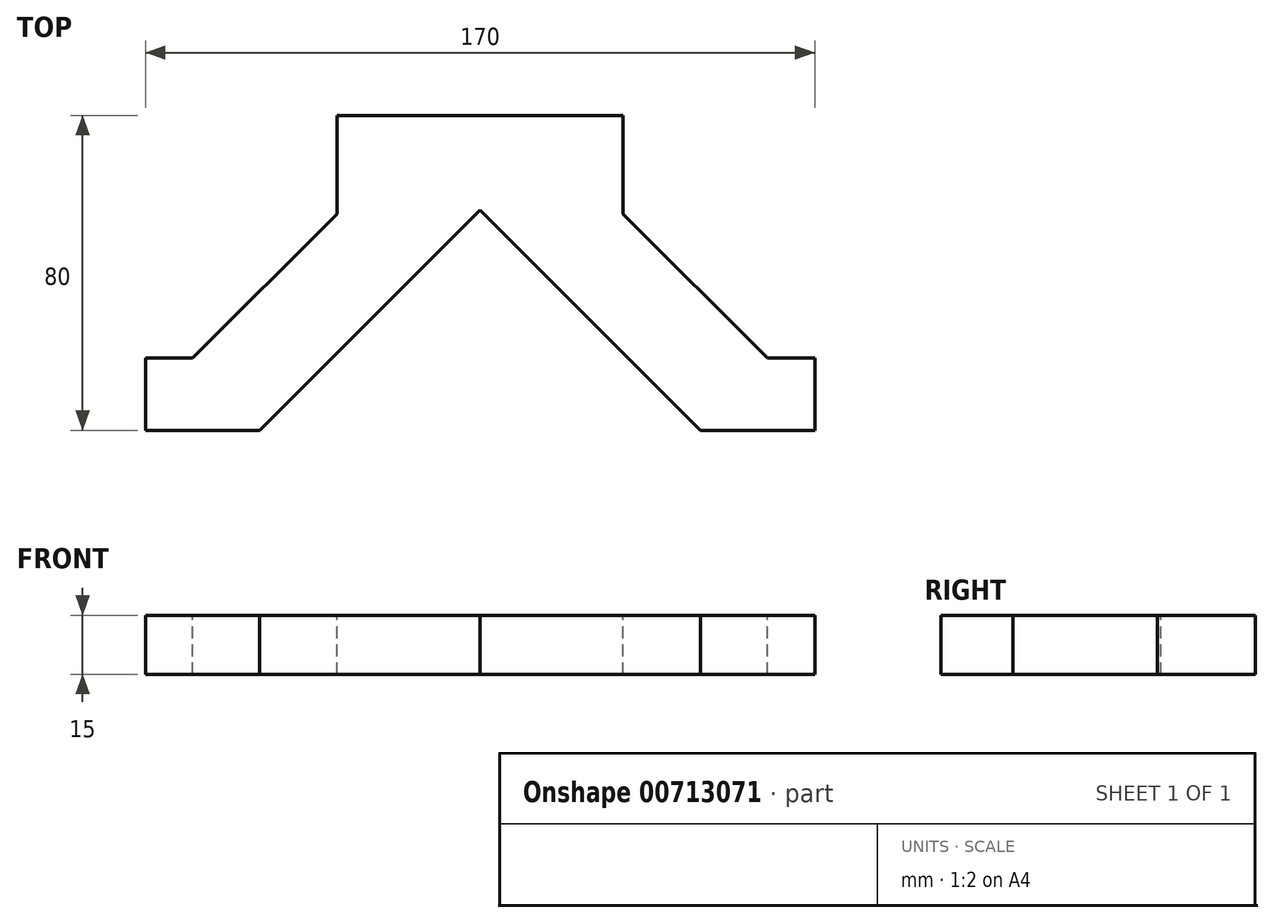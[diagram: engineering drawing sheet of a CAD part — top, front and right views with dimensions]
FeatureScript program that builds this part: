
annotation { "Feature Type Name" : "Feature", "Feature Type Description" : "" }
export const myFeature = defineFeature(function(context is Context, id is Id, definition is map)
    precondition{}
    {
        {
            var Q0;
            Q0=qCreatedBy(makeId("Top.planeOp"),FACE);
            var sketch = newSketch(context, id + "F0", { "sketchPlane" : qUnion([Q0])});
            skCircle(sketch, "E0", {"center": v(0, 0) * mm, "radius": 45 * mm});
            skSolve(sketch);
        }
        {
            var Q0;
            Q0=qCreatedBy(makeId("Top.planeOp"),FACE);
            var sketch = newSketch(context, id + "F1", { "sketchPlane" : qUnion([Q0])});
            skLineSegment(sketch, "E1.bottom", {"start": v(-85, 8.68) * mm, "end": v(85, 8.68) * mm});
            skLineSegment(sketch, "E1.top", {"start": v(-85, 88.68) * mm, "end": v(85, 88.68) * mm});
            skLineSegment(sketch, "E1.left", {"start": v(-85, 8.68) * mm, "end": v(-85, 88.68) * mm});
            skLineSegment(sketch, "E1.right", {"start": v(85, 8.68) * mm, "end": v(85, 88.68) * mm});
            skSolve(sketch);
        }
        {
            var Q0;
            Q0 = qSketchRegion(id + "F1", true);
            extrude(context, id + "F2", {"entities" : qUnion([Q0]), "depth" : 15 * mm, "offsetDistance" : 25 * mm});
        }
        {
            var Q0;
            Q0=makeQuery(id+"F2.opExtrude","CAP_FACE",FACE,{"disambiguationData":[OSD([sQuery(id+"F1.wireOp",EDGE,"E1.bottom"),sQuery(id+"F1.wireOp",EDGE,"E1.top"),sQuery(id+"F1.wireOp",EDGE,"E1.left"),sQuery(id+"F1.wireOp",EDGE,"E1.right")])],"isStart":false});
            var sketch = newSketch(context, id + "F3", { "sketchPlane" : qUnion([Q0])});
            skLineSegment(sketch, "E2", {"start": v(-56, 8.68) * mm, "end": v(0, 64.68) * mm});
            skLineSegment(sketch, "E3", {"start": v(0, 64.68) * mm, "end": v(56, 8.68) * mm});
            skLineSegment(sketch, "E4", {"start": v(56, 8.68) * mm, "end": v(-56, 8.68) * mm});
            skSolve(sketch);
        }
        {
            var Q0;
            Q0 = qSketchRegion(id + "F3", true);
            extrude(context, id + "F4", {"entities" : qUnion([Q0]), "operationType" : NewBodyOperationType.REMOVE, "oppositeDirection" : true, "depth" : 15 * mm, "offsetDistance" : 25 * mm});
        }
        {
            var Q0;
            Q0=makeQuery(id+"F2.opExtrude","CAP_FACE",FACE,{"disambiguationData":[OSD([sQuery(id+"F1.wireOp",EDGE,"E1.bottom"),sQuery(id+"F1.wireOp",EDGE,"E1.top"),sQuery(id+"F1.wireOp",EDGE,"E1.left"),sQuery(id+"F1.wireOp",EDGE,"E1.right")])],"isStart":false});
            var sketch = newSketch(context, id + "F5", { "sketchPlane" : qUnion([Q0])});
            skLineSegment(sketch, "E5", {"start": v(-85, 27.04) * mm, "end": v(-73, 27.04) * mm});
            skLineSegment(sketch, "E6", {"start": v(-73, 27.04) * mm, "end": v(-36.36, 63.68) * mm});
            skLineSegment(sketch, "E7", {"start": v(-36.36, 63.68) * mm, "end": v(-36.36, 88.68) * mm});
            skLineSegment(sketch, "E8", {"start": v(-36.36, 88.68) * mm, "end": v(36.36, 88.68) * mm});
            skLineSegment(sketch, "E9", {"start": v(36.36, 88.68) * mm, "end": v(36.36, 63.68) * mm});
            skLineSegment(sketch, "E10", {"start": v(36.36, 63.68) * mm, "end": v(73, 27.04) * mm});
            skLineSegment(sketch, "E11", {"start": v(73, 27.04) * mm, "end": v(85, 27.04) * mm});
            skLineSegment(sketch, "E12", {"start": v(85, 27.04) * mm, "end": v(85, 88.68) * mm});
            skLineSegment(sketch, "E13", {"start": v(85, 88.68) * mm, "end": v(-85, 88.68) * mm});
            skLineSegment(sketch, "E14", {"start": v(-85, 88.68) * mm, "end": v(-85, 27.04) * mm});
            skSolve(sketch);
        }
        {
            var Q0;
            Q0 = qSketchRegion(id + "F5", true);
            extrude(context, id + "F6", {"entities" : qUnion([Q0]), "operationType" : NewBodyOperationType.REMOVE, "oppositeDirection" : true, "depth" : 25 * mm, "offsetDistance" : 25 * mm});
        }
    });
